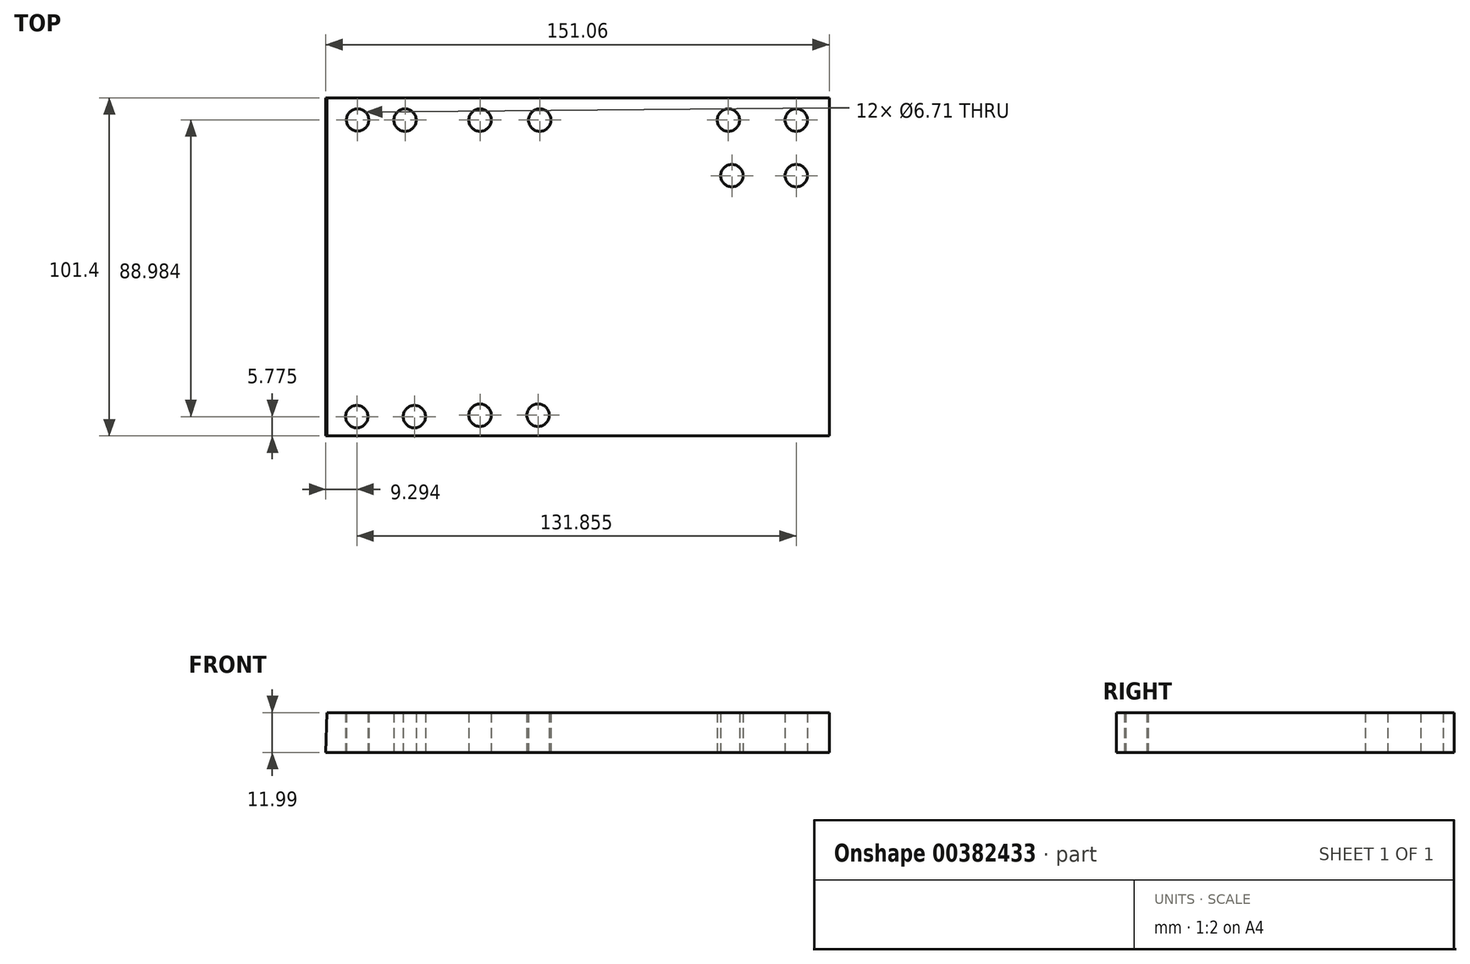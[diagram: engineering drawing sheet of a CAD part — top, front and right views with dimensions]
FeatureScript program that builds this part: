
annotation { "Feature Type Name" : "Feature", "Feature Type Description" : "" }
export const myFeature = defineFeature(function(context is Context, id is Id, definition is map)
    precondition{}
    {
        {
            var Q0;
            Q0=qCreatedBy(makeId("Front.planeOp"),FACE);
            var sketch = newSketch(context, id + "F0", { "sketchPlane" : qUnion([Q0])});
            skLineSegment(sketch, "E0", {"start": v(-85.77, 48.24) * mm, "end": v(65, 48.24) * mm});
            skLineSegment(sketch, "E1", {"start": v(65, 48.24) * mm, "end": v(65, 36.25) * mm});
            skLineSegment(sketch, "E2", {"start": v(65, 36.25) * mm, "end": v(-86.07, 36.25) * mm});
            skLineSegment(sketch, "E3", {"start": v(-86.07, 36.25) * mm, "end": v(-85.77, 48.24) * mm});
            skSolve(sketch);
        }
        {
            var Q0;
            Q0 = qSketchRegion(id + "F0", true);
            extrude(context, id + "F1", {"entities" : qUnion([Q0]), "depth" : 25.4 * mm});
        }
        {
            var Q0;
            Q0=makeQuery(id+"F1.opExtrude","CAP_FACE",FACE,{"disambiguationData":[OSD([sQuery(id+"F0.wireOp",EDGE,"E0"),sQuery(id+"F0.wireOp",EDGE,"E1"),sQuery(id+"F0.wireOp",EDGE,"E2"),sQuery(id+"F0.wireOp",EDGE,"E3")])],"isStart":false});
            extrude(context, id + "F2", {"entities" : qUnion([Q0]), "operationType" : NewBodyOperationType.ADD, "depth" : 76 * mm});
        }
        {
            var Q0;
            Q0=qCreatedBy(makeId("Top.planeOp"),FACE);
            var sketch = newSketch(context, id + "F3", { "sketchPlane" : qUnion([Q0])});
            skCircle(sketch, "E4", {"center": v(-76.53, -6.64) * mm, "radius": 3.36 * mm});
            skCircle(sketch, "E5", {"center": v(-62.3, -6.68) * mm, "radius": 3.36 * mm});
            skCircle(sketch, "E6", {"center": v(-76.78, -95.63) * mm, "radius": 3.36 * mm});
            skCircle(sketch, "E7", {"center": v(-59.51, -95.63) * mm, "radius": 3.36 * mm});
            skCircle(sketch, "E8", {"center": v(-39.81, -6.68) * mm, "radius": 3.36 * mm});
            skCircle(sketch, "E9", {"center": v(-21.88, -6.68) * mm, "radius": 3.36 * mm});
            skCircle(sketch, "E10", {"center": v(-39.81, -95.2) * mm, "radius": 3.36 * mm});
            skCircle(sketch, "E11", {"center": v(-22.4, -95.2) * mm, "radius": 3.36 * mm});
            skCircle(sketch, "E12", {"center": v(34.71, -6.68) * mm, "radius": 3.36 * mm});
            skCircle(sketch, "E13", {"center": v(55.08, -6.68) * mm, "radius": 3.36 * mm});
            skCircle(sketch, "E14", {"center": v(55.08, -23.35) * mm, "radius": 3.36 * mm});
            skCircle(sketch, "E15", {"center": v(35.77, -23.35) * mm, "radius": 3.36 * mm});
            skSolve(sketch);
        }
        {
            var Q0;
            Q0 = qSketchRegion(id + "F3", true);
            extrude(context, id + "F4", {"entities" : qUnion([Q0]), "operationType" : NewBodyOperationType.REMOVE, "depth" : 56.4 * mm});
        }
    });
